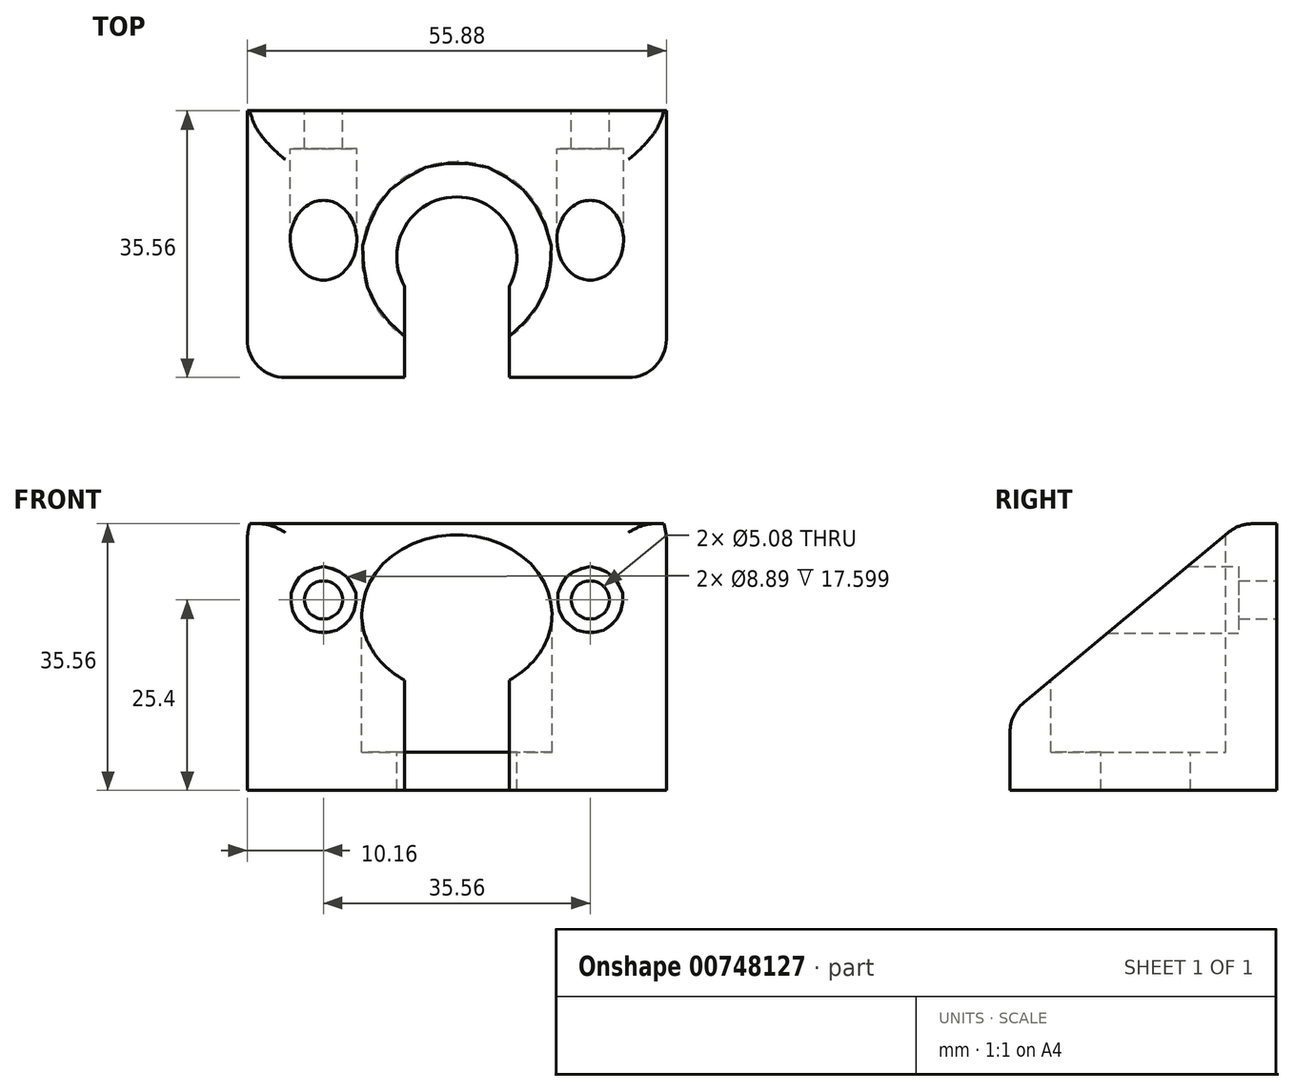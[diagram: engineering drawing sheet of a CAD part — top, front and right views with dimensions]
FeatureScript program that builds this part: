
annotation { "Feature Type Name" : "Feature", "Feature Type Description" : "" }
export const myFeature = defineFeature(function(context is Context, id is Id, definition is map)
    precondition{}
    {
        {
            var Q0;
            Q0=qCreatedBy(makeId("Right.planeOp"),FACE);
            var sketch = newSketch(context, id + "F0", { "sketchPlane" : qUnion([Q0])});
            skLineSegment(sketch, "E0.bottom", {"start": v(-16.07, 0) * mm, "end": v(19.5, 0) * mm});
            skLineSegment(sketch, "E0.top", {"start": v(14.41, 35.56) * mm, "end": v(19.5, 35.56) * mm});
            skLineSegment(sketch, "E0.left", {"start": v(-16.07, 0) * mm, "end": v(-16.07, 10.16) * mm});
            skLineSegment(sketch, "E0.right", {"start": v(19.5, 0) * mm, "end": v(19.5, 35.56) * mm});
            skLineSegment(sketch, "E1", {"start": v(14.41, 35.56) * mm, "end": v(-16.07, 10.16) * mm});
            skSolve(sketch);
        }
        {
            var Q0;
            Q0 = qSketchRegion(id + "F0", true);
            extrude(context, id + "F1", {"entities" : qUnion([Q0]), "endBound" : BoundingType.SYMMETRIC, "depth" : 55.88 * mm, "offsetDistance" : 25.4 * mm});
        }
        {
            var Q0;
            Q0=makeQuery(id+"F1.opExtrude","SWEPT_FACE",FACE,{"disambiguationData":[OSD([sQuery(id+"F0.wireOp",EDGE,"E0.top")])]});
            var sketch = newSketch(context, id + "F2", { "sketchPlane" : qUnion([Q0])});
            skCircle(sketch, "E2", {"center": v(0, 0) * mm, "radius": 12.7 * mm});
            skSolve(sketch);
        }
        {
            var Q0;
            Q0 = qSketchRegion(id + "F2", true);
            extrude(context, id + "F3", {"entities" : qUnion([Q0]), "operationType" : NewBodyOperationType.REMOVE, "oppositeDirection" : true, "depth" : 30.48 * mm, "offsetDistance" : 25.4 * mm});
        }
        {
            var Q0;
            Q0=makeQuery(id+"F3.boolean.opBoolean","COPY",FACE,{"derivedFrom":makeQuery(id+"F3.opExtrude","CAP_FACE",FACE,{"disambiguationData":[OSD([sQuery(id+"F2.wireOp",EDGE,"E2")])],"isStart":false})});
            var sketch = newSketch(context, id + "F4", { "sketchPlane" : qUnion([Q0])});
            skCircle(sketch, "E3", {"center": v(0, 0) * mm, "radius": 8 * mm});
            skSolve(sketch);
        }
        {
            var Q0;
            Q0 = qSketchRegion(id + "F4", true);
            extrude(context, id + "F5", {"entities" : qUnion([Q0]), "operationType" : NewBodyOperationType.REMOVE, "oppositeDirection" : true, "depth" : 50.8 * mm, "offsetDistance" : 25.4 * mm});
        }
        {
            var Q0;
            Q0=makeQuery(id+"F1.opExtrude","SWEPT_FACE",FACE,{"disambiguationData":[OSD([sQuery(id+"F0.wireOp",EDGE,"E0.left")])]});
            var sketch = newSketch(context, id + "F6", { "sketchPlane" : qUnion([Q0])});
            skLineSegment(sketch, "E4.bottom", {"start": v(6.99, 15.24) * mm, "end": v(-6.98, 15.24) * mm});
            skLineSegment(sketch, "E4.top", {"start": v(6.98, -15.24) * mm, "end": v(-6.99, -15.24) * mm});
            skLineSegment(sketch, "E4.left", {"start": v(6.99, 15.24) * mm, "end": v(6.98, -15.24) * mm});
            skLineSegment(sketch, "E4.right", {"start": v(-6.98, 15.24) * mm, "end": v(-6.99, -15.24) * mm});
            skPoint(sketch, "E4.middle", {"position": v(0, 0) * mm});
            skSolve(sketch);
        }
        {
            var Q0;
            Q0 = qSketchRegion(id + "F6", true);
            extrude(context, id + "F7", {"entities" : qUnion([Q0]), "operationType" : NewBodyOperationType.REMOVE, "oppositeDirection" : true, "depth" : 19.05 * mm, "offsetDistance" : 25.4 * mm});
        }
        {
            var Q0;
            {var subQ0=sQuery(id+"F0.wireOp",EDGE,"E1");var subQ1=sQuery(id+"F0.wireOp",EDGE,"E0.left");Q0=makeQuery(id+"F7.boolean.opBoolean","SPLIT",EDGE,{"disambiguationData":[TD([makeQuery(id+"F7.opExtrude","SWEPT_FACE",FACE,{"disambiguationData":[OSD([sQuery(id+"F6.wireOp",EDGE,"E4.right")])]})])],"derivedFrom":makeQuery(id+"F1.opExtrude","SWEPT_EDGE",EDGE,{"disambiguationData":[OSD([subQ1,subQ0])]})});}
            var Q1;
            {var subQ0=sQuery(id+"F0.wireOp",EDGE,"E1");var subQ1=sQuery(id+"F0.wireOp",EDGE,"E0.left");Q1=makeQuery(id+"F7.boolean.opBoolean","SPLIT",EDGE,{"disambiguationData":[TD([makeQuery(id+"F7.opExtrude","SWEPT_FACE",FACE,{"disambiguationData":[OSD([sQuery(id+"F6.wireOp",EDGE,"E4.left")])]})])],"derivedFrom":makeQuery(id+"F1.opExtrude","SWEPT_EDGE",EDGE,{"disambiguationData":[OSD([subQ1,subQ0])]})});}
            var Q2;
            Q2=makeQuery(id+"F1.opExtrude","CAP_EDGE",EDGE,{"disambiguationData":[OSD([sQuery(id+"F0.wireOp",EDGE,"E0.left")])],"isStart":false});
            var Q3;
            Q3=makeQuery(id+"F1.opExtrude","CAP_EDGE",EDGE,{"disambiguationData":[OSD([sQuery(id+"F0.wireOp",EDGE,"E1")])],"isStart":false});
            var Q4;
            Q4=makeQuery(id+"F1.opExtrude","CAP_EDGE",EDGE,{"disambiguationData":[OSD([sQuery(id+"F0.wireOp",EDGE,"E1")])],"isStart":true});
            var Q5;
            Q5=makeQuery(id+"F1.opExtrude","CAP_EDGE",EDGE,{"disambiguationData":[OSD([sQuery(id+"F0.wireOp",EDGE,"E0.left")])],"isStart":true});
            var Q6;
            Q6=makeQuery(id+"F1.opExtrude","SWEPT_EDGE",EDGE,{"disambiguationData":[OSD([sQuery(id+"F0.wireOp",EDGE,"E0.top"),sQuery(id+"F0.wireOp",EDGE,"E1")])]});
            fillet(context, id + "F8", {"entities" : qUnion([Q0, Q1, Q2, Q3, Q4, Q5, Q6]), "radius" : 5.08 * mm, "tangentPropagation" : true, "allowEdgeOverflow" : false});
        }
        {
            var Q0;
            Q0=makeQuery(id+"F1.opExtrude","SWEPT_FACE",FACE,{"disambiguationData":[OSD([sQuery(id+"F0.wireOp",EDGE,"E0.right")])]});
            var sketch = newSketch(context, id + "F9", { "sketchPlane" : qUnion([Q0])});
            skCircle(sketch, "E5", {"center": v(-17.78, 25.4) * mm, "radius": 2.54 * mm});
            skPoint(sketch, "E5.centerSnap0", {"position": v(-17.78, 33.18) * mm});
            skCircle(sketch, "E6.MirrorC", {"center": v(17.78, 25.4) * mm, "radius": 2.54 * mm});
            skSolve(sketch);
        }
        {
            var Q0;
            Q0 = qSketchRegion(id + "F9", true);
            extrude(context, id + "F10", {"entities" : qUnion([Q0]), "operationType" : NewBodyOperationType.REMOVE, "endBound" : BoundingType.UP_TO_NEXT, "oppositeDirection" : true, "depth" : 25.4 * mm, "offsetDistance" : 25.4 * mm});
        }
        {
            var Q0;
            Q0=makeQuery(id+"F1.opExtrude","SWEPT_FACE",FACE,{"disambiguationData":[OSD([sQuery(id+"F0.wireOp",EDGE,"E0.right")])]});
            cPlane(context, id + "F11", {"entities" : qUnion([Q0]), "cplaneType" : CPlaneType.OFFSET, "offset" : 5.08 * mm, "oppositeDirection" : true, "width" : 152.4 * mm, "height" : 152.4 * mm});
        }
        {
            var Q0;
            Q0=qCreatedBy(id+"F11.planeOp",FACE);
            var sketch = newSketch(context, id + "F12", { "sketchPlane" : qUnion([Q0])});
            skCircle(sketch, "E7", {"center": v(-17.78, 25.4) * mm, "radius": 4.45 * mm});
            skCircle(sketch, "E8.MirrorC", {"center": v(17.78, 25.4) * mm, "radius": 4.45 * mm});
            skSolve(sketch);
        }
        {
            var Q0;
            Q0 = qSketchRegion(id + "F12", true);
            extrude(context, id + "F13", {"entities" : qUnion([Q0]), "operationType" : NewBodyOperationType.REMOVE, "oppositeDirection" : true, "depth" : 25.4 * mm, "offsetDistance" : 25.4 * mm});
        }
    });
